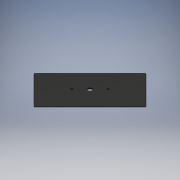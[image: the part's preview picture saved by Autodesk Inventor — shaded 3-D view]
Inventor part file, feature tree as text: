
AUTODESK INVENTOR PART (.ipt)
format: ipt  version: 2018 (Build 220112000, 112)  size: 855,040 bytes
history: native  units: mm
features: other x2, extrude x2, fillet x2, sketch x2
ambient origin geometry x8: Origin, YZ Plane, XZ Plane, XY Plane, X Axis, Y Axis, Z Axis, Center Point
bodies: Solid1 (feature_tree)
feature tree (8):
  other  "34mm_Reflector_Element"
  other  "MeshFeature1"
  extrude  "Extrusion1"  Depth=56.0mm
  extrude  "Extrusion2"  Depth=56.0mm
  fillet  "Fillet1"  Radius=3.5mm
  fillet  "Fillet2"  Radius=3.5mm
  sketch  "Sketch1"  dims[d10=55.0mm d11=56.0mm]
  sketch  "Sketch2"  dims[d12=110.0mm d13=56.0mm d14=3.5mm d15=3.5mm d17=6.0mm d18=2.0mm d19=0.0mm d20=10.0mm d21=0.0mm d22=1.0mm d23=1.0mm]
